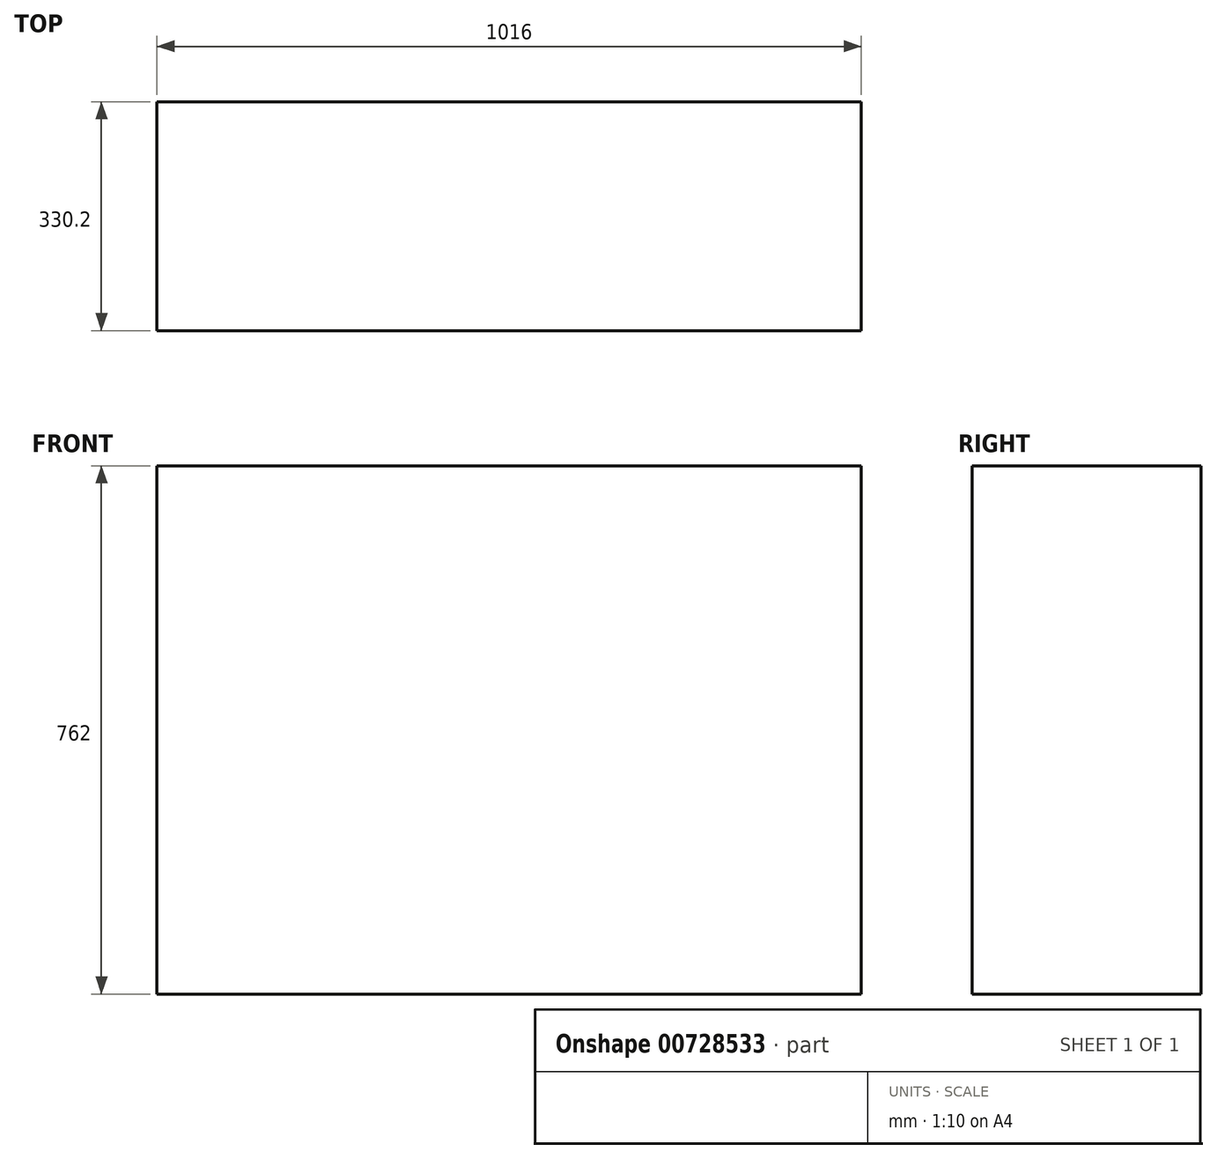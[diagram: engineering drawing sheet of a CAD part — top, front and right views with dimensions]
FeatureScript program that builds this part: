
annotation { "Feature Type Name" : "Feature", "Feature Type Description" : "" }
export const myFeature = defineFeature(function(context is Context, id is Id, definition is map)
    precondition{}
    {
        {
            var Q0;
            Q0=qCreatedBy(makeId("Top.planeOp"),FACE);
            var sketch = newSketch(context, id + "F0", { "sketchPlane" : qUnion([Q0])});
            skLineSegment(sketch, "E0.bottom", {"start": v(508, 165.1) * mm, "end": v(-508, 165.1) * mm});
            skLineSegment(sketch, "E0.top", {"start": v(508, -165.1) * mm, "end": v(-508, -165.1) * mm});
            skLineSegment(sketch, "E0.left", {"start": v(508, 165.1) * mm, "end": v(508, -165.1) * mm});
            skLineSegment(sketch, "E0.right", {"start": v(-508, 165.1) * mm, "end": v(-508, -165.1) * mm});
            skPoint(sketch, "E0.middle", {"position": v(0, 0) * mm});
            skSolve(sketch);
        }
        {
            var Q0;
            Q0 = qSketchRegion(id + "F0", true);
            extrude(context, id + "F1", {"entities" : qUnion([Q0]), "depth" : 762 * mm, "offsetDistance" : 25.4 * mm});
        }
    });
